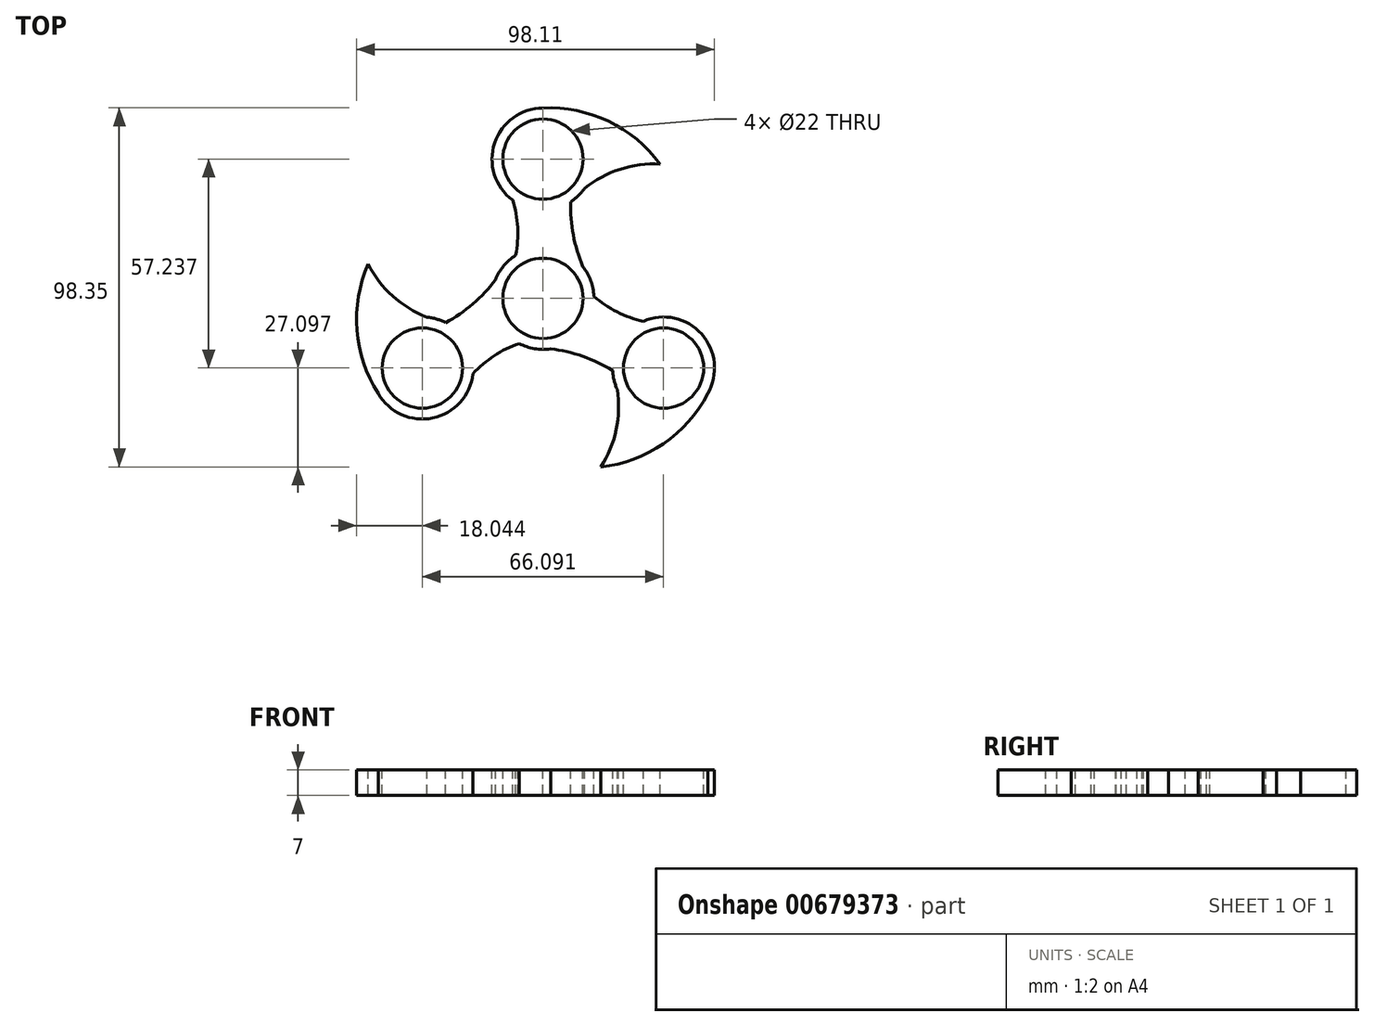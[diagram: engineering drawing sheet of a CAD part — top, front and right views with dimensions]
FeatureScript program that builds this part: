
annotation { "Feature Type Name" : "Feature", "Feature Type Description" : "" }
export const myFeature = defineFeature(function(context is Context, id is Id, definition is map)
    precondition{}
    {
        {
            var Q0;
            Q0=qCreatedBy(makeId("Top.planeOp"),FACE);
            var sketch = newSketch(context, id + "F0", { "sketchPlane" : qUnion([Q0])});
            skCircle(sketch, "E0", {"center": v(0, 45.08) * mm, "radius": 11 * mm});
            skPoint(sketch, "E1.center", {"position": v(0, 6.93) * mm});
            skCircle(sketch, "E2", {"center": v(0, 6.93) * mm, "radius": 11 * mm});
            skCircle(sketch, "E3", {"center": v(0, 6.93) * mm, "radius": 13.97 * mm});
            skCircle(sketch, "E4", {"center": v(0, 45.08) * mm, "radius": 13.97 * mm});
            skArc(sketch, "E5", {"start": v(32.08, 43.71) * mm, "mid": v(17.97, 55.42) * mm, "end": v(0, 59.05) * mm});
            skArc(sketch, "E6", {"start": v(32.08, 43.71) * mm, "mid": v(18.63, 41.34) * mm, "end": v(7.56, 33.34) * mm});
            skArc(sketch, "E7", {"start": v(7.56, 33.34) * mm, "mid": v(8.3, 24.31) * mm, "end": v(10.92, 15.64) * mm});
            skArc(sketch, "E8", {"start": v(-7.46, 18.74) * mm, "mid": v(-6.94, 26.35) * mm, "end": v(-8.32, 33.86) * mm});
            skArc(sketch, "E9.1.0", {"start": v(-6.5, -5.44) * mm, "mid": v(-13.36, -8.8) * mm, "end": v(-19.17, -13.75) * mm});
            skArc(sketch, "E9.1.1", {"start": v(-26.65, 0.27) * mm, "mid": v(-19.21, 5.43) * mm, "end": v(-13, 12.02) * mm});
            skCircle(sketch, "E9.1.2", {"center": v(-33.05, -12.15) * mm, "radius": 13.97 * mm});
            skCircle(sketch, "E9.1.3", {"center": v(-33.05, -12.15) * mm, "radius": 11 * mm});
            skArc(sketch, "E9.1.4", {"start": v(-47.9, 16.32) * mm, "mid": v(-50.98, -1.76) * mm, "end": v(-45.14, -19.14) * mm});
            skArc(sketch, "E9.1.5", {"start": v(-47.9, 16.32) * mm, "mid": v(-39.12, 5.85) * mm, "end": v(-26.65, 0.27) * mm});
            skArc(sketch, "E9.2.0", {"start": v(13.96, 7.48) * mm, "mid": v(20.3, 3.22) * mm, "end": v(27.49, 0.66) * mm});
            skArc(sketch, "E9.2.1", {"start": v(19.1, -12.83) * mm, "mid": v(10.9, -8.96) * mm, "end": v(2.09, -6.89) * mm});
            skCircle(sketch, "E9.2.2", {"center": v(33.05, -12.15) * mm, "radius": 13.97 * mm});
            skCircle(sketch, "E9.2.3", {"center": v(33.05, -12.15) * mm, "radius": 11 * mm});
            skArc(sketch, "E9.2.4", {"start": v(15.82, -39.25) * mm, "mid": v(33.01, -32.88) * mm, "end": v(45.14, -19.14) * mm});
            skArc(sketch, "E9.2.5", {"start": v(15.82, -39.25) * mm, "mid": v(20.5, -26.42) * mm, "end": v(19.1, -12.83) * mm});
            skSolve(sketch);
        }
        {
            var Q0;
            Q0 = qSketchRegion(id + "F0", true);
            extrude(context, id + "F1", {"entities" : qUnion([Q0]), "oppositeDirection" : true, "depth" : 7 * mm, "offsetDistance" : 25.4 * mm});
        }
    });
